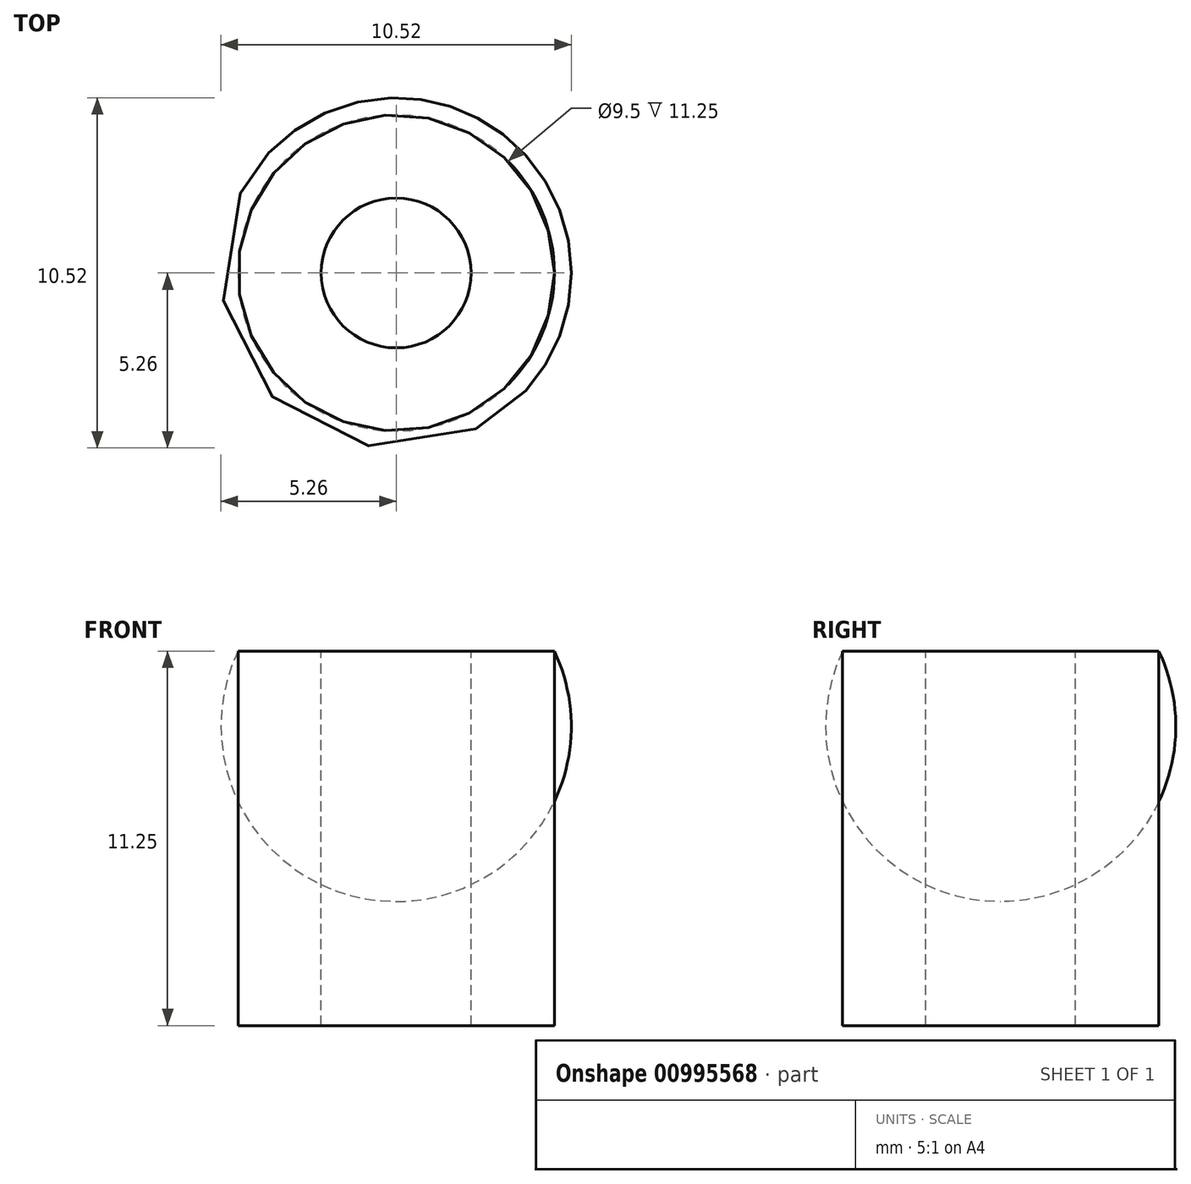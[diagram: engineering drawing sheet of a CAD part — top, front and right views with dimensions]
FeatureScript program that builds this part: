
annotation { "Feature Type Name" : "Feature", "Feature Type Description" : "" }
export const myFeature = defineFeature(function(context is Context, id is Id, definition is map)
    precondition{}
    {
        {
            var Q0;
            Q0=qCreatedBy(makeId("Top.planeOp"),FACE);
            var sketch = newSketch(context, id + "F0", { "sketchPlane" : qUnion([Q0])});
            skCircle(sketch, "E0", {"center": v(0, 0) * mm, "radius": 4.75 * mm});
            skCircle(sketch, "E1", {"center": v(0, 0) * mm, "radius": 2.25 * mm});
            skLineSegment(sketch, "E2", {"start": v(0, 0) * mm, "end": v(4.75, 0) * mm});
            skLineSegment(sketch, "E3", {"start": v(0, 0) * mm, "end": v(-4.75, 0) * mm});
            skSolve(sketch);
        }
        {
            var Q0;
            Q0=qCreatedBy(makeId("Front.planeOp"),FACE);
            var sketch = newSketch(context, id + "F1", { "sketchPlane" : qUnion([Q0])});
            skLineSegment(sketch, "E4", {"start": v(0, 0) * mm, "end": v(0, 3) * mm});
            skArc(sketch, "E5", {"start": v(4.75, 0) * mm, "mid": v(0, 3) * mm, "end": v(-4.75, 0) * mm});
            skLineSegment(sketch, "E6", {"start": v(-4.75, 0) * mm, "end": v(4.75, 0) * mm});
            skSolve(sketch);
        }
        {
            var Q0;
            {var subQ0=sQuery(id+"F1.wireOp",EDGE,"E4");Q0=makeQuery(id+"F1.imprint","IMPRINT",FACE,{"disambiguationData":[TD([[makeQuery(id+"F1.imprint","IMPRINT",EDGE,{"derivedFrom":subQ0}),1.0]])]});}
            var Q1;
            Q1=sQuery(id+"F1.wireOp",EDGE,"E5");
            var Q2;
            Q2=sQuery(id+"F1.wireOp",EDGE,"E4");
            revolve(context, id + "F2", {"surfaceOperationType" : NewSurfaceOperationType.NEW, "entities" : qUnion([Q0]), "surfaceEntities" : qUnion([Q1]), "axis" : qUnion([Q2]), "revolveType" : RevolveType.FULL});
        }
        {
            var Q0;
            {var subQ0=sQuery(id+"F0.wireOp",EDGE,"E2");var subQ1=sQuery(id+"F0.wireOp",EDGE,"E0");var subQ2=makeQuery(id+"F0.imprint","INTERSECT",VERTEX,{"derivedFrom":[subQ1,subQ0]});Q0=makeQuery(id+"F0.imprint","IMPRINT",FACE,{"disambiguationData":[TD([[makeQuery(id+"F0.imprint","IMPRINT",EDGE,{"disambiguationData":[TD([[subQ2,-1.0]])],"derivedFrom":subQ1}),1.0]])]});}
            var Q1;
            {var subQ0=sQuery(id+"F0.wireOp",EDGE,"E2");var subQ1=sQuery(id+"F0.wireOp",EDGE,"E0");var subQ2=makeQuery(id+"F0.imprint","INTERSECT",VERTEX,{"derivedFrom":[subQ1,subQ0]});Q1=makeQuery(id+"F0.imprint","IMPRINT",FACE,{"disambiguationData":[TD([[makeQuery(id+"F0.imprint","IMPRINT",EDGE,{"disambiguationData":[TD([[subQ2,1.0]])],"derivedFrom":subQ1}),1.0]])]});}
            extrude(context, id + "F3", {"entities" : qUnion([Q0, Q1]), "operationType" : NewBodyOperationType.ADD, "oppositeDirection" : true, "depth" : 11.25 * mm, "offsetDistance" : 25 * mm});
        }
    });
